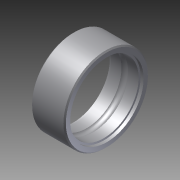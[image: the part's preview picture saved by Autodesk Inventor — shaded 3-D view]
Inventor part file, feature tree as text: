
AUTODESK INVENTOR PART (.ipt)
format: ipt  version: 2013 SP2 (Build 170200200, 200)  size: 157,184 bytes
history: native  units: mm
features: other x84, revolve x1, sketch x1
ambient origin geometry x8: Origin, YZ Plane, XZ Plane, XY Plane, X Axis, Y Axis, Z Axis, Center Point
bodies: Solid1 (feature_tree)
feature tree (86):
  revolve  "Revolution1"  [1 undecoded]
  other  "center_XY"
  other  "center_YZ"
  other  "center_ZX"
  other  "center_X"
  other  "center_Y"
  other  "center_Z"
  other  "center_Center"
  other  "or_1_1_XY"
  other  "or_1_1_YZ"
  other  "or_1_1_ZX"
  other  "or_1_1_X"
  other  "or_1_1_Y"
  other  "or_1_1_Z"
  other  "or_1_1_Center"
  other  "or_1_10_XY"
  other  "or_1_10_YZ"
  other  "or_1_10_ZX"
  other  "or_1_10_X"
  other  "or_1_10_Y"
  other  "or_1_10_Z"
  other  "or_1_10_Center"
  other  "or_1_2_XY"
  other  "or_1_2_YZ"
  other  "or_1_2_ZX"
  other  "or_1_2_X"
  other  "or_1_2_Y"
  other  "or_1_2_Z"
  other  "or_1_2_Center"
  other  "or_1_3_XY"
  other  "or_1_3_YZ"
  other  "or_1_3_ZX"
  other  "or_1_3_X"
  other  "or_1_3_Y"
  other  "or_1_3_Z"
  other  "or_1_3_Center"
  other  "or_1_4_XY"
  other  "or_1_4_YZ"
  other  "or_1_4_ZX"
  other  "or_1_4_X"
  other  "or_1_4_Y"
  other  "or_1_4_Z"
  other  "or_1_4_Center"
  other  "or_1_5_XY"
  other  "or_1_5_YZ"
  other  "or_1_5_ZX"
  other  "or_1_5_X"
  other  "or_1_5_Y"
  other  "or_1_5_Z"
  other  "or_1_5_Center"
  other  "or_1_6_XY"
  other  "or_1_6_YZ"
  other  "or_1_6_ZX"
  other  "or_1_6_X"
  other  "or_1_6_Y"
  other  "or_1_6_Z"
  other  "or_1_6_Center"
  other  "or_1_7_XY"
  other  "or_1_7_YZ"
  other  "or_1_7_ZX"
  other  "or_1_7_X"
  other  "or_1_7_Y"
  other  "or_1_7_Z"
  other  "or_1_7_Center"
  other  "or_1_8_XY"
  other  "or_1_8_YZ"
  other  "or_1_8_ZX"
  other  "or_1_8_X"
  other  "or_1_8_Y"
  other  "or_1_8_Z"
  other  "or_1_8_Center"
  other  "or_1_9_XY"
  other  "or_1_9_YZ"
  other  "or_1_9_ZX"
  other  "or_1_9_X"
  other  "or_1_9_Y"
  other  "or_1_9_Z"
  other  "or_1_9_Center"
  other  "outer_XY"
  other  "outer_YZ"
  other  "outer_ZX"
  other  "outer_X"
  other  "outer_Y"
  other  "outer_Z"
  other  "outer_Center"
  sketch  "Sketch_4"  dims[d0=360.0deg]
note: 1 required parameter value undecoded (feature->parameter linkage not recoverable at this tier; creation-order binding heuristic only, values carry confidence <= 0.55)
